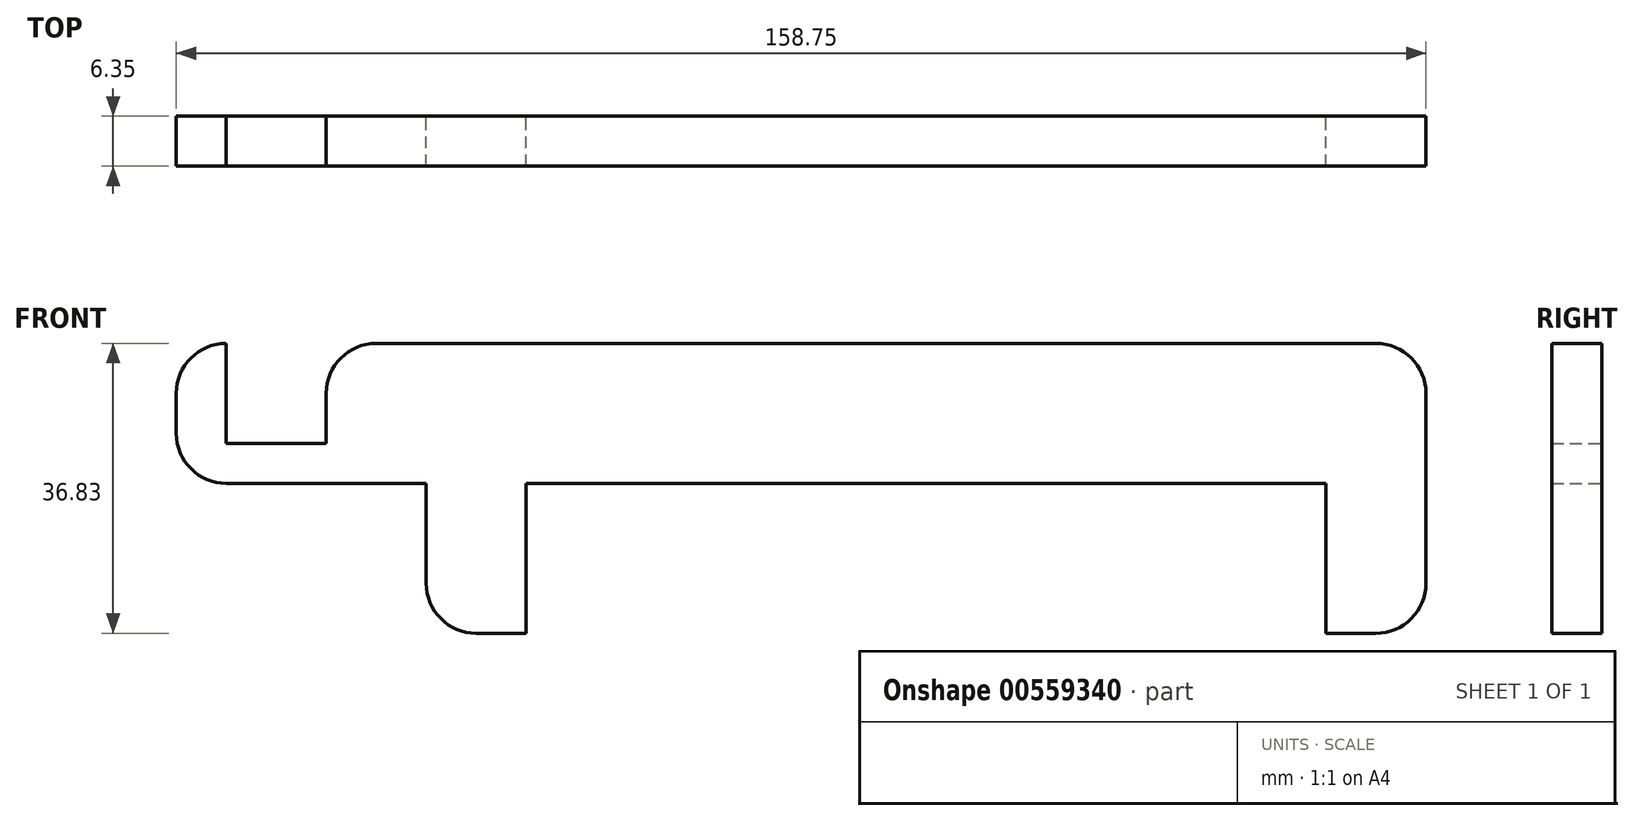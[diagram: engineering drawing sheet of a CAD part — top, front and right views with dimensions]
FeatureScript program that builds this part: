
annotation { "Feature Type Name" : "Feature", "Feature Type Description" : "" }
export const myFeature = defineFeature(function(context is Context, id is Id, definition is map)
    precondition{}
    {
        {
            var Q0;
            Q0=qCreatedBy(makeId("Front.planeOp"),FACE);
            var sketch = newSketch(context, id + "F0", { "sketchPlane" : qUnion([Q0])});
            skLineSegment(sketch, "E0", {"start": v(0, 0) * mm, "end": v(0, 19.05) * mm});
            skLineSegment(sketch, "E1", {"start": v(0, 19.05) * mm, "end": v(-101.6, 19.05) * mm});
            skLineSegment(sketch, "E2", {"start": v(-101.6, 19.05) * mm, "end": v(-101.6, 0) * mm});
            skLineSegment(sketch, "E3", {"start": v(-101.6, 0) * mm, "end": v(-107.95, 0) * mm});
            skLineSegment(sketch, "E4", {"start": v(0, 0) * mm, "end": v(6.35, 0) * mm});
            skLineSegment(sketch, "E5", {"start": v(12.7, 6.35) * mm, "end": v(12.7, 30.48) * mm});
            skLineSegment(sketch, "E6", {"start": v(6.35, 36.83) * mm, "end": v(-120.65, 36.83) * mm});
            skLineSegment(sketch, "E7", {"start": v(-127, 30.48) * mm, "end": v(-127, 24.13) * mm});
            skLineSegment(sketch, "E8", {"start": v(-127, 24.13) * mm, "end": v(-139.7, 24.13) * mm});
            skLineSegment(sketch, "E9", {"start": v(-139.7, 24.13) * mm, "end": v(-139.7, 36.83) * mm});
            skLineSegment(sketch, "E10", {"start": v(-139.7, 36.83) * mm, "end": v(-139.7, 36.83) * mm});
            skLineSegment(sketch, "E11", {"start": v(-146.05, 30.48) * mm, "end": v(-146.05, 25.4) * mm});
            skLineSegment(sketch, "E12", {"start": v(-114.3, 6.35) * mm, "end": v(-114.3, 19.05) * mm});
            skLineSegment(sketch, "E13", {"start": v(-114.3, 19.05) * mm, "end": v(-139.7, 19.05) * mm});
            skPoint(sketch, "E14.visualSharp", {"position": v(-146.05, 19.05) * mm});
            skArc(sketch, "E14.filletArc", {"start": v(-146.05, 25.4) * mm, "mid": v(-144.2, 20.9) * mm, "end": v(-139.7, 19.05) * mm});
            skPoint(sketch, "E15.visualSharp", {"position": v(-146.05, 36.83) * mm});
            skArc(sketch, "E15.filletArc", {"start": v(-139.7, 36.83) * mm, "mid": v(-144.2, 34.97) * mm, "end": v(-146.05, 30.48) * mm});
            skPoint(sketch, "E16.visualSharp", {"position": v(-114.3, 0) * mm});
            skArc(sketch, "E16.filletArc", {"start": v(-114.3, 6.35) * mm, "mid": v(-112.44, 1.86) * mm, "end": v(-107.95, 0) * mm});
            skPoint(sketch, "E17.visualSharp", {"position": v(12.7, 0) * mm});
            skArc(sketch, "E17.filletArc", {"start": v(6.35, 0) * mm, "mid": v(10.84, 1.86) * mm, "end": v(12.7, 6.35) * mm});
            skPoint(sketch, "E18.visualSharp", {"position": v(12.7, 36.83) * mm});
            skArc(sketch, "E18.filletArc", {"start": v(12.7, 30.48) * mm, "mid": v(10.84, 34.97) * mm, "end": v(6.35, 36.83) * mm});
            skPoint(sketch, "E19.visualSharp", {"position": v(-127, 36.83) * mm});
            skArc(sketch, "E19.filletArc", {"start": v(-120.65, 36.83) * mm, "mid": v(-125.14, 34.97) * mm, "end": v(-127, 30.48) * mm});
            skSolve(sketch);
        }
        {
            var Q0;
            Q0=makeQuery(id+"F0.imprint","IMPRINT",FACE,{"disambiguationData":[TD([[makeQuery(id+"F0.imprint","IMPRINT",EDGE,{"derivedFrom":sQuery(id+"F0.wireOp",EDGE,"E0")}),-1.0]])]});
            extrude(context, id + "F1", {"entities" : qUnion([Q0]), "depth" : 6.35 * mm, "offsetDistance" : 25.4 * mm});
        }
    });
